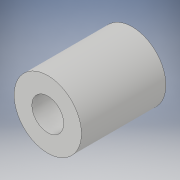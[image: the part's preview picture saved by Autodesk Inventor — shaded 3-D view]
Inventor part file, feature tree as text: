
AUTODESK INVENTOR PART (.ipt)
format: ipt  version: 2017 (Build 210142000, 142)  size: 95,232 bytes
history: native  units: in
note: dims shown in document units (in); Inventor stores cm internally (conversion verified against a paired STEP export)
features: extrude x1, sketch x1
ambient origin geometry x8: Origin, YZ Plane, XZ Plane, XY Plane, X Axis, Y Axis, Z Axis, Center Point
bodies: Solid1 (feature_tree)
feature tree (2):
  extrude  "Extrusion1"  Depth=0.69in
  sketch  "Sketch1"  dims[d0=0.26in d1=0.55in d2=0.69in d3=0.0in]
